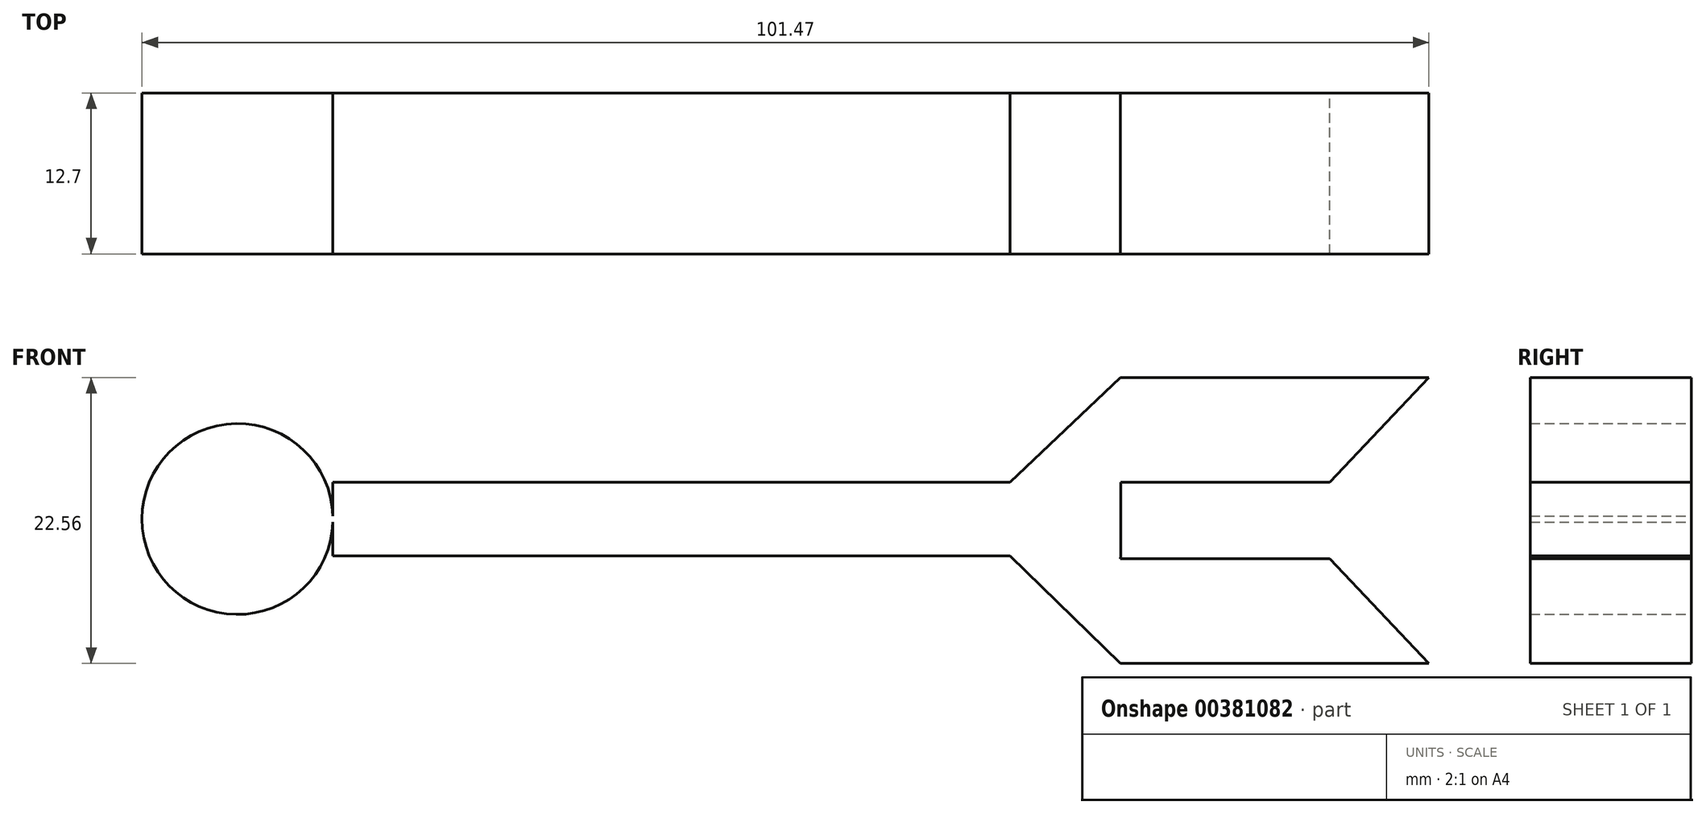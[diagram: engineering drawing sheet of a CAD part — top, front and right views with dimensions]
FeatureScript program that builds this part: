
annotation { "Feature Type Name" : "Feature", "Feature Type Description" : "" }
export const myFeature = defineFeature(function(context is Context, id is Id, definition is map)
    precondition{}
    {
        {
            var Q0;
            Q0=qCreatedBy(makeId("Front.planeOp"),FACE);
            var sketch = newSketch(context, id + "F0", { "sketchPlane" : qUnion([Q0])});
            skPoint(sketch, "E0.middle", {"position": v(0, 0) * mm});
            skCircle(sketch, "E1", {"center": v(-38.48, 0) * mm, "radius": 7.53 * mm});
            skLineSegment(sketch, "E2.bottom", {"start": v(30.96, 2.91) * mm, "end": v(-30.96, 2.91) * mm});
            skLineSegment(sketch, "E2.top", {"start": v(30.96, -2.91) * mm, "end": v(-30.96, -2.91) * mm});
            skLineSegment(sketch, "E2.left", {"start": v(30.96, 2.91) * mm, "end": v(30.96, -2.91) * mm});
            skLineSegment(sketch, "E2.right", {"start": v(-30.96, 2.91) * mm, "end": v(-30.96, -2.91) * mm});
            skLineSegment(sketch, "E3.bottom", {"start": v(47.65, 11.16) * mm, "end": v(31.14, 11.16) * mm});
            skLineSegment(sketch, "E3.top", {"start": v(47.65, 2.9) * mm, "end": v(31.14, 2.9) * mm});
            skLineSegment(sketch, "E3.left", {"start": v(47.65, 11.16) * mm, "end": v(47.65, 2.9) * mm});
            skLineSegment(sketch, "E3.right", {"start": v(31.14, 11.16) * mm, "end": v(31.14, 2.9) * mm});
            skPoint(sketch, "E3.middle", {"position": v(39.4, 7.03) * mm});
            skLineSegment(sketch, "E4.bottom", {"start": v(47.65, -11.4) * mm, "end": v(31.14, -11.4) * mm});
            skLineSegment(sketch, "E4.top", {"start": v(47.65, -3.15) * mm, "end": v(31.14, -3.15) * mm});
            skLineSegment(sketch, "E4.left", {"start": v(47.65, -11.4) * mm, "end": v(47.65, -3.15) * mm});
            skLineSegment(sketch, "E4.right", {"start": v(31.14, -11.4) * mm, "end": v(31.14, -3.15) * mm});
            skPoint(sketch, "E4.middle", {"position": v(39.4, -7.27) * mm});
            skLineSegment(sketch, "E5.bottom", {"start": v(22.43, -2.91) * mm, "end": v(31.16, -2.91) * mm});
            skLineSegment(sketch, "E5.top", {"start": v(22.43, 2.91) * mm, "end": v(31.16, 2.91) * mm});
            skLineSegment(sketch, "E5.left", {"start": v(22.43, -2.91) * mm, "end": v(22.43, 2.91) * mm});
            skLineSegment(sketch, "E5.right", {"start": v(31.16, -2.91) * mm, "end": v(31.16, 2.91) * mm});
            skPoint(sketch, "E5.middle", {"position": v(26.8, 0) * mm});
            skLineSegment(sketch, "E6", {"start": v(22.43, 2.91) * mm, "end": v(31.14, 11.16) * mm});
            skLineSegment(sketch, "E7", {"start": v(22.43, -2.91) * mm, "end": v(31.14, -11.4) * mm});
            skLineSegment(sketch, "E8", {"start": v(31.16, -2.91) * mm, "end": v(31.14, -3.15) * mm});
            skLineSegment(sketch, "E9", {"start": v(47.65, 11.16) * mm, "end": v(55.46, 11.16) * mm});
            skLineSegment(sketch, "E10", {"start": v(55.46, 11.16) * mm, "end": v(47.65, 2.9) * mm});
            skLineSegment(sketch, "E11", {"start": v(47.65, -11.4) * mm, "end": v(55.46, -11.4) * mm});
            skLineSegment(sketch, "E12", {"start": v(55.46, -11.4) * mm, "end": v(47.65, -3.15) * mm});
            skSolve(sketch);
        }
        {
            var Q0;
            Q0 = qSketchRegion(id + "F0", true);
            extrude(context, id + "F1", {"entities" : qUnion([Q0]), "depth" : 12.7 * mm, "offsetDistance" : 25.4 * mm});
        }
    });
